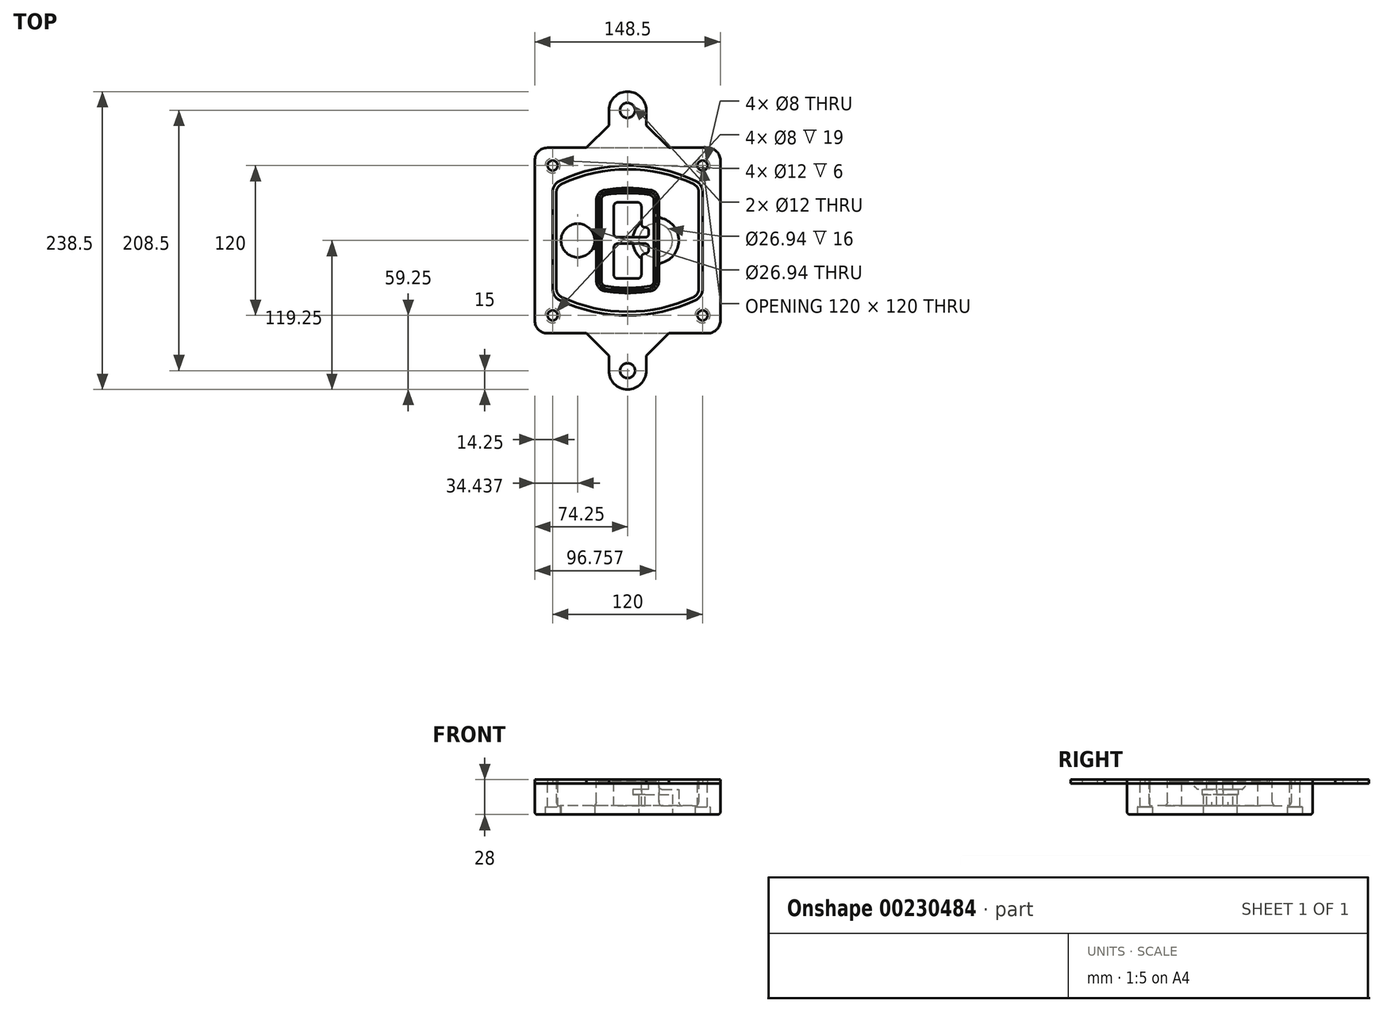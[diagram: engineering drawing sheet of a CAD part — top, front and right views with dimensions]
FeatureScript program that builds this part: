
annotation { "Feature Type Name" : "Feature", "Feature Type Description" : "" }
export const myFeature = defineFeature(function(context is Context, id is Id, definition is map)
    precondition{}
    {
        {
            var Q0;
            Q0=qCreatedBy(makeId("Top.planeOp"),FACE);
            var sketch = newSketch(context, id + "F0", { "sketchPlane" : qUnion([Q0])});
            skPoint(sketch, "E0.rect.middle", {"position": v(0, 0) * mm});
            skLineSegment(sketch, "E1.bottom", {"start": v(-64.25, -74.25) * mm, "end": v(64.25, -74.25) * mm});
            skLineSegment(sketch, "E1.top", {"start": v(-64.25, 74.25) * mm, "end": v(64.25, 74.25) * mm});
            skLineSegment(sketch, "E1.left", {"start": v(-74.25, -64.25) * mm, "end": v(-74.25, 64.25) * mm});
            skLineSegment(sketch, "E1.right", {"start": v(74.25, -64.25) * mm, "end": v(74.25, 64.25) * mm});
            skLineSegment(sketch, "E2", {"start": v(-74.25, 74.25) * mm, "end": v(74.25, -74.25) * mm, "construction": true});
            skLineSegment(sketch, "E3", {"start": v(74.25, 74.25) * mm, "end": v(-74.25, -74.25) * mm, "construction": true});
            skCircle(sketch, "E4", {"center": v(-60, 60) * mm, "radius": 4 * mm});
            skCircle(sketch, "E5", {"center": v(60, 60) * mm, "radius": 4 * mm});
            skCircle(sketch, "E6", {"center": v(60, -60) * mm, "radius": 4 * mm});
            skCircle(sketch, "E7", {"center": v(-60, -60) * mm, "radius": 4 * mm});
            skLineSegment(sketch, "E8", {"start": v(-60, 60) * mm, "end": v(60, 60) * mm, "construction": true});
            skLineSegment(sketch, "E9", {"start": v(60, 60) * mm, "end": v(60, -60) * mm, "construction": true});
            skLineSegment(sketch, "E10", {"start": v(60, -60) * mm, "end": v(-60, -60) * mm, "construction": true});
            skLineSegment(sketch, "E11", {"start": v(-60, -60) * mm, "end": v(-60, 60) * mm, "construction": true});
            skLineSegment(sketch, "E12", {"start": v(-60, 38.83) * mm, "end": v(-60, -38.83) * mm});
            skLineSegment(sketch, "E13", {"start": v(60, 38.83) * mm, "end": v(60, -38.83) * mm});
            skArc(sketch, "E14", {"start": v(54.26, 47.88) * mm, "mid": v(0, 60) * mm, "end": v(-54.26, 47.88) * mm});
            skArc(sketch, "E15", {"start": v(-54.26, -47.88) * mm, "mid": v(0, -60) * mm, "end": v(54.26, -47.88) * mm});
            skLineSegment(sketch, "E16", {"start": v(-60, 0) * mm, "end": v(60, 0) * mm, "construction": true});
            skPoint(sketch, "E17.visualSharp", {"position": v(-60, -45) * mm});
            skArc(sketch, "E17.filletArc", {"start": v(-60, -38.83) * mm, "mid": v(-58.44, -44.2) * mm, "end": v(-54.26, -47.88) * mm});
            skPoint(sketch, "E18.visualSharp", {"position": v(-60, 45) * mm});
            skArc(sketch, "E18.filletArc", {"start": v(-54.26, 47.88) * mm, "mid": v(-58.44, 44.2) * mm, "end": v(-60, 38.83) * mm});
            skPoint(sketch, "E19.visualSharp", {"position": v(60, 45) * mm});
            skArc(sketch, "E19.filletArc", {"start": v(60, 38.83) * mm, "mid": v(58.44, 44.2) * mm, "end": v(54.26, 47.88) * mm});
            skPoint(sketch, "E20.visualSharp", {"position": v(60, -45) * mm});
            skArc(sketch, "E20.filletArc", {"start": v(54.26, -47.88) * mm, "mid": v(58.44, -44.2) * mm, "end": v(60, -38.83) * mm});
            skPoint(sketch, "E21.visualSharp", {"position": v(-74.25, 74.25) * mm});
            skArc(sketch, "E21.filletArc", {"start": v(-64.25, 74.25) * mm, "mid": v(-71.32, 71.32) * mm, "end": v(-74.25, 64.25) * mm});
            skPoint(sketch, "E22.visualSharp", {"position": v(74.25, 74.25) * mm});
            skArc(sketch, "E22.filletArc", {"start": v(74.25, 64.25) * mm, "mid": v(71.32, 71.32) * mm, "end": v(64.25, 74.25) * mm});
            skPoint(sketch, "E23.visualSharp", {"position": v(74.25, -74.25) * mm});
            skArc(sketch, "E23.filletArc", {"start": v(64.25, -74.25) * mm, "mid": v(71.32, -71.32) * mm, "end": v(74.25, -64.25) * mm});
            skPoint(sketch, "E24.visualSharp", {"position": v(-74.25, -74.25) * mm});
            skArc(sketch, "E24.filletArc", {"start": v(-74.25, -64.25) * mm, "mid": v(-71.32, -71.32) * mm, "end": v(-64.25, -74.25) * mm});
            skArc(sketch, "E25.0", {"start": v(57, 38.83) * mm, "mid": v(55.9, 42.58) * mm, "end": v(52.98, 45.17) * mm});
            skLineSegment(sketch, "E25.1", {"start": v(57, 38.83) * mm, "end": v(57, -38.83) * mm});
            skArc(sketch, "E25.2", {"start": v(52.98, -45.17) * mm, "mid": v(55.9, -42.58) * mm, "end": v(57, -38.83) * mm});
            skArc(sketch, "E25.3", {"start": v(-52.98, -45.17) * mm, "mid": v(0, -57) * mm, "end": v(52.98, -45.17) * mm});
            skArc(sketch, "E25.4", {"start": v(-57, -38.83) * mm, "mid": v(-55.9, -42.58) * mm, "end": v(-52.98, -45.17) * mm});
            skArc(sketch, "E25.5", {"start": v(52.98, 45.17) * mm, "mid": v(0, 57) * mm, "end": v(-52.98, 45.17) * mm});
            skLineSegment(sketch, "E25.6", {"start": v(-57, 38.83) * mm, "end": v(-57, -38.83) * mm});
            skArc(sketch, "E25.7", {"start": v(-52.98, 45.17) * mm, "mid": v(-55.9, 42.58) * mm, "end": v(-57, 38.83) * mm});
            skArc(sketch, "E26.0", {"start": v(-55.96, 51.5) * mm, "mid": v(-61.82, 46.33) * mm, "end": v(-64, 38.83) * mm});
            skArc(sketch, "E26.1", {"start": v(55.96, 51.5) * mm, "mid": v(0, 64) * mm, "end": v(-55.96, 51.5) * mm});
            skArc(sketch, "E26.2", {"start": v(64, 38.83) * mm, "mid": v(61.82, 46.33) * mm, "end": v(55.96, 51.5) * mm});
            skLineSegment(sketch, "E26.3", {"start": v(64, 38.83) * mm, "end": v(64, -38.83) * mm});
            skArc(sketch, "E26.4", {"start": v(55.96, -51.5) * mm, "mid": v(61.82, -46.33) * mm, "end": v(64, -38.83) * mm});
            skLineSegment(sketch, "E26.5", {"start": v(-64, 38.83) * mm, "end": v(-64, -38.83) * mm});
            skArc(sketch, "E26.6", {"start": v(-55.96, -51.5) * mm, "mid": v(0, -64) * mm, "end": v(55.96, -51.5) * mm});
            skArc(sketch, "E26.7", {"start": v(-64, -38.83) * mm, "mid": v(-61.82, -46.33) * mm, "end": v(-55.96, -51.5) * mm});
            skSolve(sketch);
        }
        {
            var Q0;
            Q0=makeQuery(id+"F0.imprint","IMPRINT",FACE,{"disambiguationData":[TD([[makeQuery(id+"F0.imprint","IMPRINT",EDGE,{"derivedFrom":sQuery(id+"F0.wireOp",EDGE,"E1.bottom")}),1.0]])]});
            var Q1;
            Q1=makeQuery(id+"F0.imprint","IMPRINT",FACE,{"disambiguationData":[TD([[makeQuery(id+"F0.imprint","IMPRINT",EDGE,{"derivedFrom":sQuery(id+"F0.wireOp",EDGE,"E12")}),1.0]])]});
            var Q2;
            Q2=makeQuery(id+"F0.imprint","IMPRINT",FACE,{"disambiguationData":[TD([[makeQuery(id+"F0.imprint","IMPRINT",EDGE,{"derivedFrom":sQuery(id+"F0.wireOp",EDGE,"E25.0")}),1.0]])]});
            var Q3;
            Q3=makeQuery(id+"F0.imprint","IMPRINT",FACE,{"disambiguationData":[TD([[makeQuery(id+"F0.imprint","IMPRINT",EDGE,{"derivedFrom":sQuery(id+"F0.wireOp",EDGE,"E12")}),-1.0]])]});
            extrude(context, id + "F1", {"entities" : qUnion([Q0, Q1, Q2, Q3]), "oppositeDirection" : true, "depth" : 25 * mm});
        }
        {
            var Q0;
            Q0=makeQuery(id+"F0.imprint","IMPRINT",FACE,{"disambiguationData":[TD([[makeQuery(id+"F0.imprint","IMPRINT",EDGE,{"derivedFrom":sQuery(id+"F0.wireOp",EDGE,"E12")}),1.0]])]});
            extrude(context, id + "F2", {"entities" : qUnion([Q0]), "operationType" : NewBodyOperationType.ADD, "depth" : 3 * mm});
        }
        {
            var Q0;
            Q0=makeQuery(id+"F0.imprint","IMPRINT",FACE,{"disambiguationData":[TD([[makeQuery(id+"F0.imprint","IMPRINT",EDGE,{"derivedFrom":sQuery(id+"F0.wireOp",EDGE,"E25.0")}),1.0]])]});
            extrude(context, id + "F3", {"entities" : qUnion([Q0]), "operationType" : NewBodyOperationType.REMOVE, "oppositeDirection" : true, "depth" : 18 * mm});
        }
        {
            var Q0;
            Q0=makeQuery(id+"F2.opExtrude","CAP_FACE",FACE,{"disambiguationData":[OSD([sQuery(id+"F0.wireOp",EDGE,"E12"),sQuery(id+"F0.wireOp",EDGE,"E13"),sQuery(id+"F0.wireOp",EDGE,"E14"),sQuery(id+"F0.wireOp",EDGE,"E15"),sQuery(id+"F0.wireOp",EDGE,"E17.filletArc"),sQuery(id+"F0.wireOp",EDGE,"E18.filletArc"),sQuery(id+"F0.wireOp",EDGE,"E19.filletArc"),sQuery(id+"F0.wireOp",EDGE,"E20.filletArc"),sQuery(id+"F0.wireOp",EDGE,"E25.0"),sQuery(id+"F0.wireOp",EDGE,"E25.1"),sQuery(id+"F0.wireOp",EDGE,"E25.2"),sQuery(id+"F0.wireOp",EDGE,"E25.3"),sQuery(id+"F0.wireOp",EDGE,"E25.4"),sQuery(id+"F0.wireOp",EDGE,"E25.5"),sQuery(id+"F0.wireOp",EDGE,"E25.6"),sQuery(id+"F0.wireOp",EDGE,"E25.7")])],"isStart":false});
            var sketch = newSketch(context, id + "F4", { "sketchPlane" : qUnion([Q0])});
            skArc(sketch, "E27.0", {"start": v(-18.34, -40.45) * mm, "mid": v(0, -42) * mm, "end": v(18.34, -40.45) * mm});
            skArc(sketch, "E28.0", {"start": v(18.34, 40.45) * mm, "mid": v(0, 42) * mm, "end": v(-18.34, 40.45) * mm});
            skLineSegment(sketch, "E29", {"start": v(-25, 32.57) * mm, "end": v(-25, -32.57) * mm});
            skLineSegment(sketch, "E30", {"start": v(25, 32.57) * mm, "end": v(25, -32.57) * mm});
            skLineSegment(sketch, "E31", {"start": v(-25, 39.1) * mm, "end": v(25, 39.1) * mm, "construction": true});
            skLineSegment(sketch, "E32", {"start": v(-25, -39.1) * mm, "end": v(25, -39.1) * mm, "construction": true});
            skPoint(sketch, "E33.visualSharp", {"position": v(-25, 39.1) * mm});
            skArc(sketch, "E33.filletArc", {"start": v(-18.34, 40.45) * mm, "mid": v(-23.11, 37.73) * mm, "end": v(-25, 32.57) * mm});
            skPoint(sketch, "E34.visualSharp", {"position": v(25, 39.1) * mm});
            skArc(sketch, "E34.filletArc", {"start": v(25, 32.57) * mm, "mid": v(23.11, 37.73) * mm, "end": v(18.34, 40.45) * mm});
            skPoint(sketch, "E35.visualSharp", {"position": v(25, -39.1) * mm});
            skArc(sketch, "E35.filletArc", {"start": v(18.34, -40.45) * mm, "mid": v(23.11, -37.73) * mm, "end": v(25, -32.57) * mm});
            skPoint(sketch, "E36.visualSharp", {"position": v(-25, -39.1) * mm});
            skArc(sketch, "E36.filletArc", {"start": v(-25, -32.57) * mm, "mid": v(-23.11, -37.73) * mm, "end": v(-18.34, -40.45) * mm});
            skArc(sketch, "E37.0", {"start": v(52.98, 45.17) * mm, "mid": v(0, 57) * mm, "end": v(-52.98, 45.17) * mm});
            skArc(sketch, "E37.1", {"start": v(-52.98, 45.17) * mm, "mid": v(-55.9, 42.58) * mm, "end": v(-57, 38.83) * mm});
            skLineSegment(sketch, "E37.2", {"start": v(-57, 38.83) * mm, "end": v(-57, -38.83) * mm});
            skArc(sketch, "E37.3", {"start": v(-57, -38.83) * mm, "mid": v(-55.9, -42.58) * mm, "end": v(-52.98, -45.17) * mm});
            skArc(sketch, "E37.4", {"start": v(-52.98, -45.17) * mm, "mid": v(0, -57) * mm, "end": v(52.98, -45.17) * mm});
            skArc(sketch, "E37.5", {"start": v(52.98, -45.17) * mm, "mid": v(55.9, -42.58) * mm, "end": v(57, -38.83) * mm});
            skLineSegment(sketch, "E37.6", {"start": v(57, 38.83) * mm, "end": v(57, -38.83) * mm});
            skArc(sketch, "E37.7", {"start": v(57, 38.83) * mm, "mid": v(55.9, 42.58) * mm, "end": v(52.98, 45.17) * mm});
            skLineSegment(sketch, "E38.0", {"start": v(23, 32.57) * mm, "end": v(23, -32.57) * mm});
            skArc(sketch, "E38.1", {"start": v(18, -38.48) * mm, "mid": v(21.58, -36.44) * mm, "end": v(23, -32.57) * mm});
            skArc(sketch, "E38.2", {"start": v(-18, -38.48) * mm, "mid": v(0, -40) * mm, "end": v(18, -38.48) * mm});
            skArc(sketch, "E38.3", {"start": v(-23, -32.57) * mm, "mid": v(-21.58, -36.44) * mm, "end": v(-18, -38.48) * mm});
            skLineSegment(sketch, "E38.4", {"start": v(-23, 32.57) * mm, "end": v(-23, -32.57) * mm});
            skArc(sketch, "E38.5", {"start": v(23, 32.57) * mm, "mid": v(21.58, 36.44) * mm, "end": v(18, 38.48) * mm});
            skArc(sketch, "E38.6", {"start": v(-18, 38.48) * mm, "mid": v(-21.58, 36.44) * mm, "end": v(-23, 32.57) * mm});
            skArc(sketch, "E38.7", {"start": v(18, 38.48) * mm, "mid": v(0, 40) * mm, "end": v(-18, 38.48) * mm});
            skArc(sketch, "E39.0", {"start": v(21, 32.57) * mm, "mid": v(20.06, 35.15) * mm, "end": v(17.67, 36.5) * mm});
            skLineSegment(sketch, "E39.1", {"start": v(21, 32.57) * mm, "end": v(21, -32.57) * mm});
            skArc(sketch, "E39.2", {"start": v(17.67, -36.5) * mm, "mid": v(20.06, -35.15) * mm, "end": v(21, -32.57) * mm});
            skArc(sketch, "E39.3", {"start": v(-17.67, -36.5) * mm, "mid": v(0, -38) * mm, "end": v(17.67, -36.5) * mm});
            skArc(sketch, "E39.4", {"start": v(-21, -32.57) * mm, "mid": v(-20.06, -35.15) * mm, "end": v(-17.67, -36.5) * mm});
            skArc(sketch, "E39.5", {"start": v(17.67, 36.5) * mm, "mid": v(0, 38) * mm, "end": v(-17.67, 36.5) * mm});
            skLineSegment(sketch, "E39.6", {"start": v(-21, 32.57) * mm, "end": v(-21, -32.57) * mm});
            skArc(sketch, "E39.7", {"start": v(-17.67, 36.5) * mm, "mid": v(-20.06, 35.15) * mm, "end": v(-21, 32.57) * mm});
            skLineSegment(sketch, "E40", {"start": v(-25, 0) * mm, "end": v(25, 0) * mm, "construction": true});
            skLineSegment(sketch, "E41", {"start": v(-11, 5.5) * mm, "end": v(-11, 27.5) * mm});
            skLineSegment(sketch, "E42", {"start": v(-8, 30.5) * mm, "end": v(8, 30.5) * mm});
            skLineSegment(sketch, "E43", {"start": v(11, 27.5) * mm, "end": v(11, 13.5) * mm});
            skLineSegment(sketch, "E44", {"start": v(14, 10.5) * mm, "end": v(14, 10.5) * mm});
            skLineSegment(sketch, "E45", {"start": v(17, 7.5) * mm, "end": v(17, 5.5) * mm});
            skLineSegment(sketch, "E46", {"start": v(14, 2.5) * mm, "end": v(-8, 2.5) * mm});
            skPoint(sketch, "E47.visualSharp", {"position": v(-11, 30.5) * mm});
            skArc(sketch, "E47.filletArc", {"start": v(-8, 30.5) * mm, "mid": v(-10.12, 29.62) * mm, "end": v(-11, 27.5) * mm});
            skPoint(sketch, "E48.visualSharp", {"position": v(11, 30.5) * mm});
            skArc(sketch, "E48.filletArc", {"start": v(11, 27.5) * mm, "mid": v(10.12, 29.62) * mm, "end": v(8, 30.5) * mm});
            skPoint(sketch, "E49.visualSharp", {"position": v(11, 10.5) * mm});
            skArc(sketch, "E49.filletArc", {"start": v(11, 13.5) * mm, "mid": v(11.88, 11.38) * mm, "end": v(14, 10.5) * mm});
            skPoint(sketch, "E50.visualSharp", {"position": v(17, 10.5) * mm});
            skArc(sketch, "E50.filletArc", {"start": v(17, 7.5) * mm, "mid": v(16.12, 9.62) * mm, "end": v(14, 10.5) * mm});
            skPoint(sketch, "E51.visualSharp", {"position": v(17, 2.5) * mm});
            skArc(sketch, "E51.filletArc", {"start": v(14, 2.5) * mm, "mid": v(16.12, 3.38) * mm, "end": v(17, 5.5) * mm});
            skPoint(sketch, "E52.visualSharp", {"position": v(-11, 2.5) * mm});
            skArc(sketch, "E52.filletArc", {"start": v(-11, 5.5) * mm, "mid": v(-10.12, 3.38) * mm, "end": v(-8, 2.5) * mm});
            skLineSegment(sketch, "E53.0.MirrorCS", {"start": v(14, -2.5) * mm, "end": v(-8, -2.5) * mm});
            skArc(sketch, "E54.0.MirrorCS", {"start": v(-11, -5.5) * mm, "mid": v(-10.12, -3.38) * mm, "end": v(-8, -2.5) * mm});
            skLineSegment(sketch, "E55.0.MirrorCS", {"start": v(-11, -5.5) * mm, "end": v(-11, -27.5) * mm});
            skArc(sketch, "E56.0.MirrorCS", {"start": v(-8, -30.5) * mm, "mid": v(-10.12, -29.62) * mm, "end": v(-11, -27.5) * mm});
            skLineSegment(sketch, "E57.0.MirrorCS", {"start": v(-8, -30.5) * mm, "end": v(8, -30.5) * mm});
            skArc(sketch, "E58.0.MirrorCS", {"start": v(11, -27.5) * mm, "mid": v(10.12, -29.62) * mm, "end": v(8, -30.5) * mm});
            skLineSegment(sketch, "E59.0.MirrorCS", {"start": v(11, -27.5) * mm, "end": v(11, -13.5) * mm});
            skArc(sketch, "E60.0.MirrorCS", {"start": v(11, -13.5) * mm, "mid": v(11.88, -11.38) * mm, "end": v(14, -10.5) * mm});
            skArc(sketch, "E61.0.MirrorCS", {"start": v(17, -7.5) * mm, "mid": v(16.12, -9.62) * mm, "end": v(14, -10.5) * mm});
            skLineSegment(sketch, "E62.0.MirrorCS", {"start": v(17, -7.5) * mm, "end": v(17, -5.5) * mm});
            skArc(sketch, "E63.0.MirrorCS", {"start": v(14, -2.5) * mm, "mid": v(16.12, -3.38) * mm, "end": v(17, -5.5) * mm});
            skSolve(sketch);
        }
        {
            var Q0;
            Q0=makeQuery(id+"F4.imprint","IMPRINT",FACE,{"disambiguationData":[TD([[makeQuery(id+"F4.imprint","IMPRINT",EDGE,{"derivedFrom":sQuery(id+"F4.wireOp",EDGE,"E27.0")}),1.0]])]});
            var Q1;
            Q1=makeQuery(id+"F4.imprint","IMPRINT",FACE,{"disambiguationData":[TD([[makeQuery(id+"F4.imprint","IMPRINT",EDGE,{"derivedFrom":sQuery(id+"F4.wireOp",EDGE,"E38.0")}),-1.0]])]});
            var Q2;
            Q2=makeQuery(id+"F4.imprint","IMPRINT",FACE,{"disambiguationData":[TD([[makeQuery(id+"F4.imprint","IMPRINT",EDGE,{"derivedFrom":sQuery(id+"F4.wireOp",EDGE,"E39.0")}),1.0]])]});
            extrude(context, id + "F5", {"entities" : qUnion([Q0, Q1, Q2]), "operationType" : NewBodyOperationType.ADD, "endBound" : BoundingType.UP_TO_NEXT, "oppositeDirection" : true, "depth" : 25 * mm});
        }
        {
            var Q0;
            Q0=makeQuery(id+"F4.imprint","IMPRINT",FACE,{"disambiguationData":[TD([[makeQuery(id+"F4.imprint","IMPRINT",EDGE,{"derivedFrom":sQuery(id+"F4.wireOp",EDGE,"E38.0")}),-1.0]])]});
            extrude(context, id + "F6", {"entities" : qUnion([Q0]), "operationType" : NewBodyOperationType.REMOVE, "oppositeDirection" : true, "depth" : 2 * mm});
        }
        {
            var Q0;
            Q0=makeQuery(id+"F1.opExtrude","CAP_FACE",FACE,{"disambiguationData":[OSD([sQuery(id+"F0.wireOp",EDGE,"E1.bottom"),sQuery(id+"F0.wireOp",EDGE,"E1.top"),sQuery(id+"F0.wireOp",EDGE,"E1.left"),sQuery(id+"F0.wireOp",EDGE,"E1.right"),sQuery(id+"F0.wireOp",EDGE,"E4"),sQuery(id+"F0.wireOp",EDGE,"E5"),sQuery(id+"F0.wireOp",EDGE,"E6"),sQuery(id+"F0.wireOp",EDGE,"E7"),sQuery(id+"F0.wireOp",EDGE,"E21.filletArc"),sQuery(id+"F0.wireOp",EDGE,"E22.filletArc"),sQuery(id+"F0.wireOp",EDGE,"E23.filletArc"),sQuery(id+"F0.wireOp",EDGE,"E24.filletArc")])],"isStart":false});
            var sketch = newSketch(context, id + "F7", { "sketchPlane" : qUnion([Q0])});
            skCircle(sketch, "E64", {"center": v(22.5, 0) * mm, "radius": 13.47 * mm});
            skCircle(sketch, "E65", {"center": v(-39.81, 0) * mm, "radius": 13.47 * mm});
            skLineSegment(sketch, "E66", {"start": v(74.25, 0) * mm, "end": v(-74.25, 0) * mm});
            skCircle(sketch, "E67", {"center": v(22.5, 0) * mm, "radius": 18.47 * mm});
            skCircle(sketch, "E68", {"center": v(60, -60) * mm, "radius": 6 * mm});
            skCircle(sketch, "E69", {"center": v(-60, -60) * mm, "radius": 6 * mm});
            skCircle(sketch, "E70", {"center": v(-60, 60) * mm, "radius": 6 * mm});
            skCircle(sketch, "E71", {"center": v(60, 60) * mm, "radius": 6 * mm});
            skSolve(sketch);
        }
        {
            var Q0;
            {var subQ1=sQuery(id+"F7.wireOp",EDGE,"E66");var subQ4=sQuery(id+"F7.wireOp",EDGE,"E64");var subQ6=makeQuery(id+"F7.imprint","INTERSECT",VERTEX,{"disambiguationData":[OD(0.0)],"derivedFrom":[subQ4,subQ1]});Q0=makeQuery(id+"F7.imprint","IMPRINT",FACE,{"disambiguationData":[TD([[makeQuery(id+"F7.imprint","IMPRINT",EDGE,{"disambiguationData":[TD([[subQ6,-1.0]])],"derivedFrom":subQ4}),-1.0]])]});}
            var Q1;
            {var subQ0=sQuery(id+"F7.wireOp",EDGE,"E66");var subQ1=sQuery(id+"F7.wireOp",EDGE,"E64");var subQ3=makeQuery(id+"F7.imprint","INTERSECT",VERTEX,{"disambiguationData":[OD(0.0)],"derivedFrom":[subQ1,subQ0]});Q1=makeQuery(id+"F7.imprint","IMPRINT",FACE,{"disambiguationData":[TD([[makeQuery(id+"F7.imprint","IMPRINT",EDGE,{"disambiguationData":[TD([[subQ3,-1.0]])],"derivedFrom":subQ1}),1.0]])]});}
            var Q2;
            {var subQ0=sQuery(id+"F7.wireOp",EDGE,"E66");var subQ1=sQuery(id+"F7.wireOp",EDGE,"E64");var subQ3=makeQuery(id+"F7.imprint","INTERSECT",VERTEX,{"disambiguationData":[OD(0.0)],"derivedFrom":[subQ1,subQ0]});Q2=makeQuery(id+"F7.imprint","IMPRINT",FACE,{"disambiguationData":[TD([[makeQuery(id+"F7.imprint","IMPRINT",EDGE,{"disambiguationData":[TD([[subQ3,1.0]])],"derivedFrom":subQ1}),1.0]])]});}
            var Q3;
            {var subQ1=sQuery(id+"F7.wireOp",EDGE,"E66");var subQ4=sQuery(id+"F7.wireOp",EDGE,"E64");var subQ6=makeQuery(id+"F7.imprint","INTERSECT",VERTEX,{"disambiguationData":[OD(0.0)],"derivedFrom":[subQ4,subQ1]});Q3=makeQuery(id+"F7.imprint","IMPRINT",FACE,{"disambiguationData":[TD([[makeQuery(id+"F7.imprint","IMPRINT",EDGE,{"disambiguationData":[TD([[subQ6,1.0]])],"derivedFrom":subQ4}),-1.0]])]});}
            extrude(context, id + "F8", {"entities" : qUnion([Q0, Q1, Q2, Q3]), "operationType" : NewBodyOperationType.ADD, "oppositeDirection" : true, "depth" : 20 * mm});
        }
        {
            var Q0;
            {var subQ0=sQuery(id+"F7.wireOp",EDGE,"E66");var subQ1=sQuery(id+"F7.wireOp",EDGE,"E64");var subQ3=makeQuery(id+"F7.imprint","INTERSECT",VERTEX,{"disambiguationData":[OD(0.0)],"derivedFrom":[subQ1,subQ0]});Q0=makeQuery(id+"F7.imprint","IMPRINT",FACE,{"disambiguationData":[TD([[makeQuery(id+"F7.imprint","IMPRINT",EDGE,{"disambiguationData":[TD([[subQ3,-1.0]])],"derivedFrom":subQ1}),1.0]])]});}
            var Q1;
            {var subQ0=sQuery(id+"F7.wireOp",EDGE,"E66");var subQ1=sQuery(id+"F7.wireOp",EDGE,"E64");var subQ3=makeQuery(id+"F7.imprint","INTERSECT",VERTEX,{"disambiguationData":[OD(0.0)],"derivedFrom":[subQ1,subQ0]});Q1=makeQuery(id+"F7.imprint","IMPRINT",FACE,{"disambiguationData":[TD([[makeQuery(id+"F7.imprint","IMPRINT",EDGE,{"disambiguationData":[TD([[subQ3,1.0]])],"derivedFrom":subQ1}),1.0]])]});}
            extrude(context, id + "F9", {"entities" : qUnion([Q0, Q1]), "operationType" : NewBodyOperationType.REMOVE, "oppositeDirection" : true, "depth" : 16 * mm});
        }
        {
            var Q0;
            {var subQ0=sQuery(id+"F7.wireOp",EDGE,"E66");var subQ1=sQuery(id+"F7.wireOp",EDGE,"E65");var subQ3=makeQuery(id+"F7.imprint","INTERSECT",VERTEX,{"disambiguationData":[OD(0.0)],"derivedFrom":[subQ1,subQ0]});Q0=makeQuery(id+"F7.imprint","IMPRINT",FACE,{"disambiguationData":[TD([[makeQuery(id+"F7.imprint","IMPRINT",EDGE,{"disambiguationData":[TD([[subQ3,-1.0]])],"derivedFrom":subQ1}),1.0]])]});}
            var Q1;
            {var subQ0=sQuery(id+"F7.wireOp",EDGE,"E66");var subQ1=sQuery(id+"F7.wireOp",EDGE,"E65");var subQ3=makeQuery(id+"F7.imprint","INTERSECT",VERTEX,{"disambiguationData":[OD(0.0)],"derivedFrom":[subQ1,subQ0]});Q1=makeQuery(id+"F7.imprint","IMPRINT",FACE,{"disambiguationData":[TD([[makeQuery(id+"F7.imprint","IMPRINT",EDGE,{"disambiguationData":[TD([[subQ3,1.0]])],"derivedFrom":subQ1}),1.0]])]});}
            extrude(context, id + "F10", {"entities" : qUnion([Q0, Q1]), "operationType" : NewBodyOperationType.REMOVE, "oppositeDirection" : true, "depth" : 25 * mm});
        }
        {
            var Q0;
            Q0=makeQuery(id+"F7.imprint","IMPRINT",FACE,{"disambiguationData":[TD([[makeQuery(id+"F7.imprint","IMPRINT",EDGE,{"derivedFrom":sQuery(id+"F7.wireOp",EDGE,"E68")}),1.0]])]});
            var Q1;
            Q1=makeQuery(id+"F7.imprint","IMPRINT",FACE,{"disambiguationData":[TD([[makeQuery(id+"F7.imprint","IMPRINT",EDGE,{"derivedFrom":makeQuery(id+"F1.opExtrude","CAP_EDGE",EDGE,{"disambiguationData":[OSD([sQuery(id+"F0.wireOp",EDGE,"E5")])],"isStart":false})}),-1.0]])]});
            var Q2;
            Q2=makeQuery(id+"F7.imprint","IMPRINT",FACE,{"disambiguationData":[TD([[makeQuery(id+"F7.imprint","IMPRINT",EDGE,{"derivedFrom":sQuery(id+"F7.wireOp",EDGE,"E69")}),1.0]])]});
            var Q3;
            Q3=makeQuery(id+"F7.imprint","IMPRINT",FACE,{"disambiguationData":[TD([[makeQuery(id+"F7.imprint","IMPRINT",EDGE,{"derivedFrom":makeQuery(id+"F1.opExtrude","CAP_EDGE",EDGE,{"disambiguationData":[OSD([sQuery(id+"F0.wireOp",EDGE,"E4")])],"isStart":false})}),-1.0]])]});
            var Q4;
            Q4=makeQuery(id+"F7.imprint","IMPRINT",FACE,{"disambiguationData":[TD([[makeQuery(id+"F7.imprint","IMPRINT",EDGE,{"derivedFrom":sQuery(id+"F7.wireOp",EDGE,"E70")}),1.0]])]});
            var Q5;
            Q5=makeQuery(id+"F7.imprint","IMPRINT",FACE,{"disambiguationData":[TD([[makeQuery(id+"F7.imprint","IMPRINT",EDGE,{"derivedFrom":makeQuery(id+"F1.opExtrude","CAP_EDGE",EDGE,{"disambiguationData":[OSD([sQuery(id+"F0.wireOp",EDGE,"E7")])],"isStart":false})}),-1.0]])]});
            var Q6;
            Q6=makeQuery(id+"F7.imprint","IMPRINT",FACE,{"disambiguationData":[TD([[makeQuery(id+"F7.imprint","IMPRINT",EDGE,{"derivedFrom":sQuery(id+"F7.wireOp",EDGE,"E71")}),1.0]])]});
            var Q7;
            Q7=makeQuery(id+"F7.imprint","IMPRINT",FACE,{"disambiguationData":[TD([[makeQuery(id+"F7.imprint","IMPRINT",EDGE,{"derivedFrom":makeQuery(id+"F1.opExtrude","CAP_EDGE",EDGE,{"disambiguationData":[OSD([sQuery(id+"F0.wireOp",EDGE,"E6")])],"isStart":false})}),-1.0]])]});
            extrude(context, id + "F11", {"entities" : qUnion([Q0, Q1, Q2, Q3, Q4, Q5, Q6, Q7]), "operationType" : NewBodyOperationType.REMOVE, "oppositeDirection" : true, "depth" : 6 * mm});
        }
        {
            var Q0;
            Q0=makeQuery(id+"F9.boolean.opBoolean","COPY",FACE,{"derivedFrom":makeQuery(id+"F9.opExtrude","CAP_FACE",FACE,{"disambiguationData":[OSD([sQuery(id+"F7.wireOp",EDGE,"E64")])],"isStart":false})});
            var sketch = newSketch(context, id + "F12", { "sketchPlane" : qUnion([Q0])});
            skArc(sketch, "E72.0", {"start": v(11, 14.45) * mm, "mid": v(6.45, 9.13) * mm, "end": v(4.2, 2.5) * mm});
            skArc(sketch, "E72.1", {"start": v(4.2, -2.5) * mm, "mid": v(6.45, -9.13) * mm, "end": v(11, -14.45) * mm});
            skLineSegment(sketch, "E73", {"start": v(4.2, -2.5) * mm, "end": v(14, -2.5) * mm});
            skLineSegment(sketch, "E74.0", {"start": v(14, 2.5) * mm, "end": v(4.2, 2.5) * mm});
            skArc(sketch, "E74.1", {"start": v(14, 2.5) * mm, "mid": v(16.12, 3.38) * mm, "end": v(17, 5.5) * mm});
            skLineSegment(sketch, "E74.2", {"start": v(17, 7.5) * mm, "end": v(17, 5.5) * mm});
            skArc(sketch, "E74.3", {"start": v(17, 7.5) * mm, "mid": v(16.12, 9.62) * mm, "end": v(14, 10.5) * mm});
            skArc(sketch, "E74.4", {"start": v(11, 13.5) * mm, "mid": v(11.88, 11.38) * mm, "end": v(14, 10.5) * mm});
            skLineSegment(sketch, "E74.5", {"start": v(11, 14.45) * mm, "end": v(11, 13.5) * mm});
            skLineSegment(sketch, "E74.7", {"start": v(14, -2.5) * mm, "end": v(4.2, -2.5) * mm});
            skArc(sketch, "E74.8", {"start": v(14, -2.5) * mm, "mid": v(16.12, -3.38) * mm, "end": v(17, -5.5) * mm});
            skLineSegment(sketch, "E74.9", {"start": v(17, -7.5) * mm, "end": v(17, -5.5) * mm});
            skArc(sketch, "E74.10", {"start": v(17, -7.5) * mm, "mid": v(16.12, -9.62) * mm, "end": v(14, -10.5) * mm});
            skArc(sketch, "E74.11", {"start": v(11, -13.5) * mm, "mid": v(11.88, -11.38) * mm, "end": v(14, -10.5) * mm});
            skLineSegment(sketch, "E74.12", {"start": v(11, -14.45) * mm, "end": v(11, -13.5) * mm});
            skPoint(sketch, "E75.orphan", {"position": v(11, -27.5) * mm});
            skPoint(sketch, "E76.orphan", {"position": v(-8, -2.5) * mm});
            skPoint(sketch, "E77.orphan", {"position": v(-8, 2.5) * mm});
            skPoint(sketch, "E78.orphan", {"position": v(11, 27.5) * mm});
            skSolve(sketch);
        }
        {
            var Q0;
            {var subQ7=sQuery(id+"F12.wireOp",EDGE,"E72.0");var subQ14=sQuery(id+"F12.wireOp",EDGE,"E72.1");var subQ16=sQuery(id+"F12.wireOp",EDGE,"E74.1");var subQ18=sQuery(id+"F12.wireOp",EDGE,"E74.8");Q0=qUnion([makeQuery(id+"F12.imprint","IMPRINT",FACE,{"disambiguationData":[TD([[makeQuery(id+"F12.imprint","IMPRINT",EDGE,{"derivedFrom":subQ7}),1.0]])]}),makeQuery(id+"F12.imprint","IMPRINT",FACE,{"disambiguationData":[TD([[makeQuery(id+"F12.imprint","IMPRINT",EDGE,{"derivedFrom":subQ14}),1.0]])]}),makeQuery(id+"F12.imprint","IMPRINT",FACE,{"disambiguationData":[TD([[makeQuery(id+"F12.imprint","IMPRINT",EDGE,{"derivedFrom":subQ16}),1.0]])]}),makeQuery(id+"F12.imprint","IMPRINT",FACE,{"disambiguationData":[TD([[makeQuery(id+"F12.imprint","IMPRINT",EDGE,{"derivedFrom":subQ18}),-1.0]])]})]);}
            var Q1;
            Q1=makeQuery(id+"F5.boolean.opBoolean","SPLIT",FACE,{"disambiguationData":[TD([makeQuery(id+"F5.opExtrude","SWEPT_FACE",FACE,{"disambiguationData":[OSD([sQuery(id+"F4.wireOp",EDGE,"E41")])]})])],"derivedFrom":makeQuery(id+"F3.boolean.opBoolean","COPY",FACE,{"derivedFrom":makeQuery(id+"F3.opExtrude","CAP_FACE",FACE,{"disambiguationData":[OSD([sQuery(id+"F0.wireOp",EDGE,"E25.0"),sQuery(id+"F0.wireOp",EDGE,"E25.1"),sQuery(id+"F0.wireOp",EDGE,"E25.2"),sQuery(id+"F0.wireOp",EDGE,"E25.3"),sQuery(id+"F0.wireOp",EDGE,"E25.4"),sQuery(id+"F0.wireOp",EDGE,"E25.5"),sQuery(id+"F0.wireOp",EDGE,"E25.6"),sQuery(id+"F0.wireOp",EDGE,"E25.7")])],"isStart":false})})});
            extrude(context, id + "F13", {"entities" : qUnion([Q0]), "operationType" : NewBodyOperationType.REMOVE, "endBound" : BoundingType.UP_TO_SURFACE, "endBoundEntityFace" : qUnion([Q1]), "depth" : 25 * mm});
        }
        {
            var Q0;
            Q0=makeQuery(id+"F3.boolean.opBoolean","COPY",EDGE,{"derivedFrom":makeQuery(id+"F3.opExtrude","CAP_EDGE",EDGE,{"disambiguationData":[OSD([sQuery(id+"F0.wireOp",EDGE,"E25.6")])],"isStart":false})});
            var Q1;
            Q1=makeQuery(id+"F8.boolean.opBoolean","INTERSECT",EDGE,{"derivedFrom":[makeQuery(id+"F5.opExtrude","SWEPT_FACE",FACE,{"disambiguationData":[OSD([sQuery(id+"F4.wireOp",EDGE,"E30")])]}),makeQuery(id+"F8.opExtrude","CAP_FACE",FACE,{"disambiguationData":[OSD([sQuery(id+"F7.wireOp",EDGE,"E67")])],"isStart":false})]});
            var Q2;
            Q2=makeQuery(id+"F8.boolean.opBoolean","INTERSECT",EDGE,{"disambiguationData":[OD(1.0)],"derivedFrom":[makeQuery(id+"F5.opExtrude","SWEPT_FACE",FACE,{"disambiguationData":[OSD([sQuery(id+"F4.wireOp",EDGE,"E30")])]}),makeQuery(id+"F8.opExtrude","SWEPT_FACE",FACE,{"disambiguationData":[OSD([sQuery(id+"F7.wireOp",EDGE,"E67")])]})]});
            var Q3;
            {var subQ0=sQuery(id+"F4.wireOp",EDGE,"E30");Q3=makeQuery(id+"F8.boolean.opBoolean","SPLIT",EDGE,{"disambiguationData":[TD([makeQuery(id+"F5.opExtrude","SWEPT_FACE",FACE,{"disambiguationData":[OSD([sQuery(id+"F4.wireOp",EDGE,"E35.filletArc")])]})])],"derivedFrom":makeQuery(id+"F5.opExtrude","CAP_EDGE",EDGE,{"disambiguationData":[OSD([subQ0])],"isStart":false})});}
            var Q4;
            {var subQ0=sQuery(id+"F0.wireOp",EDGE,"E25.7");var subQ1=sQuery(id+"F0.wireOp",EDGE,"E25.1");var subQ2=sQuery(id+"F0.wireOp",EDGE,"E25.6");var subQ3=sQuery(id+"F0.wireOp",EDGE,"E25.5");var subQ4=sQuery(id+"F0.wireOp",EDGE,"E25.4");var subQ5=sQuery(id+"F0.wireOp",EDGE,"E25.0");var subQ6=sQuery(id+"F0.wireOp",EDGE,"E25.2");var subQ7=sQuery(id+"F0.wireOp",EDGE,"E25.3");Q4=makeQuery(id+"F8.boolean.opBoolean","INTERSECT",EDGE,{"derivedFrom":[makeQuery(id+"F5.boolean.opBoolean","SPLIT",FACE,{"disambiguationData":[TD([makeQuery(id+"F2.opExtrude","SWEPT_FACE",FACE,{"disambiguationData":[OSD([subQ5])]})])],"derivedFrom":makeQuery(id+"F3.boolean.opBoolean","COPY",FACE,{"derivedFrom":makeQuery(id+"F3.opExtrude","CAP_FACE",FACE,{"disambiguationData":[OSD([subQ5,subQ1,subQ6,subQ7,subQ4,subQ3,subQ2,subQ0])],"isStart":false})})}),makeQuery(id+"F8.opExtrude","SWEPT_FACE",FACE,{"disambiguationData":[OSD([sQuery(id+"F7.wireOp",EDGE,"E67")])]})]});}
            var Q5;
            Q5=makeQuery(id+"F8.boolean.opBoolean","INTERSECT",EDGE,{"disambiguationData":[OD(0.0)],"derivedFrom":[makeQuery(id+"F5.opExtrude","SWEPT_FACE",FACE,{"disambiguationData":[OSD([sQuery(id+"F4.wireOp",EDGE,"E30")])]}),makeQuery(id+"F8.opExtrude","SWEPT_FACE",FACE,{"disambiguationData":[OSD([sQuery(id+"F7.wireOp",EDGE,"E67")])]})]});
            fillet(context, id + "F14", {"entities" : qUnion([Q0, Q1, Q2, Q3, Q4, Q5]), "radius" : 3 * mm, "tangentPropagation" : true, "allowEdgeOverflow" : false});
        }
        {
            var Q0;
            Q0=makeQuery(id+"F1.opExtrude","CAP_EDGE",EDGE,{"disambiguationData":[OSD([sQuery(id+"F0.wireOp",EDGE,"E1.bottom")])],"isStart":false});
            fillet(context, id + "F15", {"entities" : qUnion([Q0]), "radius" : 2 * mm, "tangentPropagation" : true, "allowEdgeOverflow" : false});
        }
        {
            var Q0;
            {var subQ0=sQuery(id+"F0.wireOp",EDGE,"E22.filletArc");var subQ1=sQuery(id+"F0.wireOp",EDGE,"E7");var subQ2=sQuery(id+"F0.wireOp",EDGE,"E6");var subQ3=sQuery(id+"F0.wireOp",EDGE,"E5");var subQ4=sQuery(id+"F0.wireOp",EDGE,"E4");var subQ5=sQuery(id+"F0.wireOp",EDGE,"E1.bottom");var subQ6=sQuery(id+"F0.wireOp",EDGE,"E21.filletArc");var subQ7=sQuery(id+"F0.wireOp",EDGE,"E1.top");var subQ8=sQuery(id+"F0.wireOp",EDGE,"E1.left");var subQ9=sQuery(id+"F0.wireOp",EDGE,"E1.right");var subQ10=sQuery(id+"F0.wireOp",EDGE,"E23.filletArc");var subQ11=sQuery(id+"F0.wireOp",EDGE,"E24.filletArc");Q0=makeQuery(id+"F2.boolean.opBoolean","SPLIT",FACE,{"disambiguationData":[TD([makeQuery(id+"F1.opExtrude","SWEPT_FACE",FACE,{"disambiguationData":[OSD([subQ5])]})])],"derivedFrom":makeQuery(id+"F1.opExtrude","CAP_FACE",FACE,{"disambiguationData":[OSD([subQ5,subQ7,subQ8,subQ9,subQ4,subQ3,subQ2,subQ1,subQ6,subQ0,subQ10,subQ11])],"isStart":true})});}
            var sketch = newSketch(context, id + "F16", { "sketchPlane" : qUnion([Q0])});
            skPoint(sketch, "E79.endSnap0", {"position": v(0, 74.25) * mm});
            skCircle(sketch, "E80", {"center": v(0, 104.25) * mm, "radius": 6 * mm});
            skLineSegment(sketch, "E81", {"start": v(15, 104.25) * mm, "end": v(15, 92.25) * mm});
            skLineSegment(sketch, "E82", {"start": v(15, 92.25) * mm, "end": v(33, 74.25) * mm});
            skLineSegment(sketch, "E83", {"start": v(0, 74.25) * mm, "end": v(0, 104.25) * mm, "construction": true});
            skArc(sketch, "E84", {"start": v(15, 104.25) * mm, "mid": v(0, 119.25) * mm, "end": v(-15, 104.25) * mm});
            skLineSegment(sketch, "E85", {"start": v(-15, 104.25) * mm, "end": v(-15, 92.25) * mm});
            skLineSegment(sketch, "E86", {"start": v(-33, 74.25) * mm, "end": v(-15, 92.25) * mm});
            skLineSegment(sketch, "E87", {"start": v(-74.25, 0) * mm, "end": v(74.25, 0) * mm, "construction": true});
            skLineSegment(sketch, "E88.MirrorCS", {"start": v(-33, -74.25) * mm, "end": v(-15, -92.25) * mm});
            skLineSegment(sketch, "E89.MirrorCS", {"start": v(-15, -104.25) * mm, "end": v(-15, -92.25) * mm});
            skLineSegment(sketch, "E90.MirrorCS", {"start": v(15, -104.25) * mm, "end": v(15, -92.25) * mm});
            skCircle(sketch, "E91.MirrorC", {"center": v(0, -104.25) * mm, "radius": 6 * mm});
            skLineSegment(sketch, "E92.MirrorCS", {"start": v(15, -92.25) * mm, "end": v(33, -74.25) * mm});
            skArc(sketch, "E93.MirrorCS", {"start": v(15, -104.25) * mm, "mid": v(0, -119.25) * mm, "end": v(-15, -104.25) * mm});
            skSolve(sketch);
        }
        {
            var Q0;
            Q0=makeQuery(id+"F16.imprint","IMPRINT",FACE,{"disambiguationData":[TD([[makeQuery(id+"F16.imprint","IMPRINT",EDGE,{"derivedFrom":sQuery(id+"F16.wireOp",EDGE,"E80")}),-1.0]])]});
            var Q1;
            {var subQ0=sQuery(id+"F16.wireOp",EDGE,"E88.MirrorCS");Q1=makeQuery(id+"F16.imprint","IMPRINT",FACE,{"disambiguationData":[TD([[makeQuery(id+"F16.imprint","IMPRINT",EDGE,{"derivedFrom":subQ0}),1.0]])]});}
            var Q2;
            Q2=makeQuery(id+"F16.imprint","IMPRINT",FACE,{"disambiguationData":[TD([[makeQuery(id+"F16.imprint","IMPRINT",EDGE,{"derivedFrom":makeQuery(id+"F1.opExtrude","CAP_EDGE",EDGE,{"disambiguationData":[OSD([sQuery(id+"F0.wireOp",EDGE,"E1.left")])],"isStart":true})}),-1.0]])]});
            var Q3;
            Q3=makeQuery(id+"F2.opExtrude","CAP_FACE",FACE,{"disambiguationData":[OSD([sQuery(id+"F0.wireOp",EDGE,"E12"),sQuery(id+"F0.wireOp",EDGE,"E13"),sQuery(id+"F0.wireOp",EDGE,"E14"),sQuery(id+"F0.wireOp",EDGE,"E15"),sQuery(id+"F0.wireOp",EDGE,"E17.filletArc"),sQuery(id+"F0.wireOp",EDGE,"E18.filletArc"),sQuery(id+"F0.wireOp",EDGE,"E19.filletArc"),sQuery(id+"F0.wireOp",EDGE,"E20.filletArc"),sQuery(id+"F0.wireOp",EDGE,"E25.0"),sQuery(id+"F0.wireOp",EDGE,"E25.1"),sQuery(id+"F0.wireOp",EDGE,"E25.2"),sQuery(id+"F0.wireOp",EDGE,"E25.3"),sQuery(id+"F0.wireOp",EDGE,"E25.4"),sQuery(id+"F0.wireOp",EDGE,"E25.5"),sQuery(id+"F0.wireOp",EDGE,"E25.6"),sQuery(id+"F0.wireOp",EDGE,"E25.7")])],"isStart":false});
            extrude(context, id + "F17", {"entities" : qUnion([Q0, Q1, Q2]), "endBound" : BoundingType.UP_TO_SURFACE, "endBoundEntityFace" : qUnion([Q3]), "depth" : 25 * mm});
        }
    });
